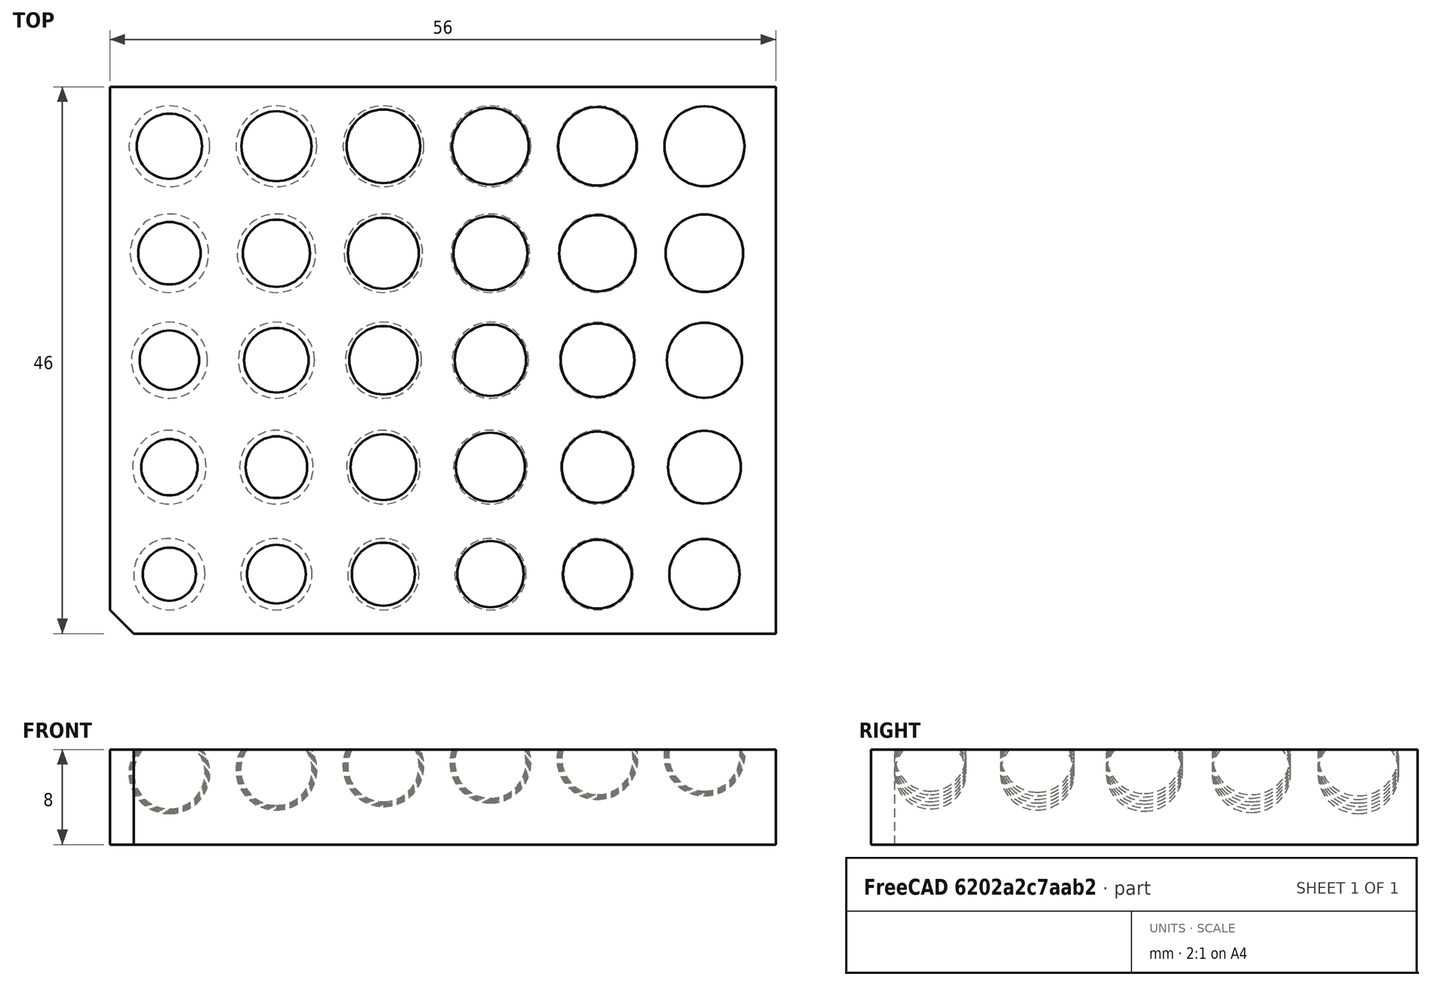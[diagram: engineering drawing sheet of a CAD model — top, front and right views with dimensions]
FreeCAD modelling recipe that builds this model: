
FCSTD DOCUMENT  (FreeCAD 0.18.4R)
Label: ball-socket-test
License: All rights reserved
LicenseURL: http://en.wikipedia.org/wiki/All_rights_reserved
objects: Part::Cut×30, Part::Feature×25, Part::Sphere×5, Part::Box×1, Part::Chamfer×1
note: 62 computed .brp shape members not serialized (recipe doc carries the construction recipe); baked Part::Feature solids carry a one-line shape summary decoded from their .brp

FEATURE [Part::Feature] Sphere006002
  Placement = pos=(18,9,6.6) rot=(0,0,1;0rad)
  shape: bbox 6.2 x 6.2 x 6.2 mm, 1 faces (baked)
FEATURE [Part::Feature] Sphere006001
  Placement = pos=(9,9,6.3) rot=(0,0,1;0rad)
  shape: bbox 6.2 x 6.2 x 6.2 mm, 1 faces (baked)
FEATURE [Part::Feature] Sphere005
  Placement = pos=(45,0,7.5) rot=(0,0,1;0rad)
  shape: bbox 6 x 6 x 6 mm, 1 faces (baked)
FEATURE [Part::Feature] Sphere001
  Placement = pos=(9,0,6.3) rot=(0,0,1;0rad)
  shape: bbox 6 x 6 x 6 mm, 1 faces (baked)
FEATURE [Part::Feature] Sphere002
  Placement = pos=(18,0,6.6) rot=(0,0,1;0rad)
  shape: bbox 6 x 6 x 6 mm, 1 faces (baked)
FEATURE [Part::Feature] Sphere004
  Placement = pos=(36,0,7.2) rot=(0,0,1;0rad)
  shape: bbox 6 x 6 x 6 mm, 1 faces (baked)
FEATURE [Part::Feature] Sphere003
  Placement = pos=(27,0,6.9) rot=(0,0,1;0rad)
  shape: bbox 6 x 6 x 6 mm, 1 faces (baked)
FEATURE [Part::Sphere] Sphere
  Angle1 = -90
  Angle2 = 90
  Angle3 = 360
  AttacherType = Attacher::AttachEngine3D
  Placement = pos=(0,0,6) rot=(0,0,1;0rad)
  Radius = 3
FEATURE [Part::Box] Box112015002017004007003  label="Cube089"
  AttacherType = Attacher::AttachEngine3D
  Height = 8
  Length = 56
  Placement = pos=(-5,-5,0) rot=(0,0,1;0rad)
  Width = 46
FEATURE [Part::Cut] Cut175
  Base = -> Box112015002017004007003
  Tool = -> Sphere
FEATURE [Part::Sphere] Sphere006
  Angle1 = -90
  Angle2 = 90
  Angle3 = 360
  AttacherType = Attacher::AttachEngine3D
  Placement = pos=(0,9,6) rot=(0,0,1;0rad)
  Radius = 3.1
FEATURE [Part::Feature] Sphere006003
  Placement = pos=(27,9,6.9) rot=(0,0,1;0rad)
  shape: bbox 6.2 x 6.2 x 6.2 mm, 1 faces (baked)
FEATURE [Part::Feature] Sphere006004
  Placement = pos=(36,9,7.2) rot=(0,0,1;0rad)
  shape: bbox 6.2 x 6.2 x 6.2 mm, 1 faces (baked)
FEATURE [Part::Feature] Sphere006005
  Placement = pos=(45,9,7.5) rot=(0,0,1;0rad)
  shape: bbox 6.2 x 6.2 x 6.2 mm, 1 faces (baked)
FEATURE [Part::Sphere] Sphere006006
  Angle1 = -90
  Angle2 = 90
  Angle3 = 360
  AttacherType = Attacher::AttachEngine3D
  Placement = pos=(0,18,6) rot=(0,0,1;0rad)
  Radius = 3.2
FEATURE [Part::Feature] Sphere006006001 .. Sphere006006005  x5 (patterned run collapsed; names and placements below)
  shape: bbox 6.4 x 6.4 x 6.4 mm, 1 faces (baked)
  placements: 5 in arithmetic series — first pos=(9,18,6.3) rot=(0,0,1;0rad), step (9,0,0.3), last pos=(45,18,7.5) rot=(0,0,1;0rad)
FEATURE [Part::Sphere] Sphere006006006
  Angle1 = -90
  Angle2 = 90
  Angle3 = 360
  AttacherType = Attacher::AttachEngine3D
  Placement = pos=(0,27,6) rot=(0,0,1;0rad)
  Radius = 3.3
FEATURE [Part::Feature] Sphere006006006001 .. Sphere006006006005  x5 (patterned run collapsed; names and placements below)
  shape: bbox 6.6 x 6.6 x 6.6 mm, 1 faces (baked)
  placements: 5 in arithmetic series — first pos=(9,27,6.3) rot=(0,0,1;0rad), step (9,0,0.3), last pos=(45,27,7.5) rot=(0,0,1;0rad)
FEATURE [Part::Sphere] Sphere006006006006
  Angle1 = -90
  Angle2 = 90
  Angle3 = 360
  AttacherType = Attacher::AttachEngine3D
  Placement = pos=(0,36,6) rot=(0,0,1;0rad)
  Radius = 3.4
FEATURE [Part::Feature] Sphere006006006006001 .. Sphere006006006006005  x5 (patterned run collapsed; names and placements below)
  shape: bbox 6.8 x 6.8 x 6.8 mm, 1 faces (baked)
  placements: 5 in arithmetic series — first pos=(9,36,6.3) rot=(0,0,1;0rad), step (9,0,0.3), last pos=(45,36,7.5) rot=(0,0,1;0rad)
FEATURE [Part::Cut] Cut176
  Base = -> Cut175
  Tool = -> Sphere006006006006005
FEATURE [Part::Cut] Cut177
  Base = -> Cut176
  Tool = -> Sphere006006006006004
FEATURE [Part::Cut] Cut178
  Base = -> Cut177
  Tool = -> Sphere006006006006003
FEATURE [Part::Cut] Cut179
  Base = -> Cut178
  Tool = -> Sphere006006006006002
FEATURE [Part::Cut] Cut180
  Base = -> Cut179
  Tool = -> Sphere006006006006001
FEATURE [Part::Cut] Cut181
  Base = -> Cut180
  Tool = -> Sphere006006006006
FEATURE [Part::Cut] Cut182
  Base = -> Cut181
  Tool = -> Sphere006006006005
FEATURE [Part::Cut] Cut183
  Base = -> Cut182
  Tool = -> Sphere006006006004
FEATURE [Part::Cut] Cut184
  Base = -> Cut183
  Tool = -> Sphere006006006003
FEATURE [Part::Cut] Cut185
  Base = -> Cut184
  Tool = -> Sphere006006006002
FEATURE [Part::Cut] Cut186
  Base = -> Cut185
  Tool = -> Sphere006006006001
FEATURE [Part::Cut] Cut187
  Base = -> Cut186
  Tool = -> Sphere006006006
FEATURE [Part::Cut] Cut188
  Base = -> Cut187
  Tool = -> Sphere006006005
FEATURE [Part::Cut] Cut189
  Base = -> Cut188
  Tool = -> Sphere006006004
FEATURE [Part::Cut] Cut190
  Base = -> Cut189
  Tool = -> Sphere006006003
FEATURE [Part::Cut] Cut191
  Base = -> Cut190
  Tool = -> Sphere006006002
FEATURE [Part::Cut] Cut192
  Base = -> Cut191
  Tool = -> Sphere006006001
FEATURE [Part::Cut] Cut193
  Base = -> Cut192
  Tool = -> Sphere006006
FEATURE [Part::Cut] Cut194
  Base = -> Cut193
  Tool = -> Sphere006005
FEATURE [Part::Cut] Cut195
  Base = -> Cut194
  Tool = -> Sphere006004
FEATURE [Part::Cut] Cut196
  Base = -> Cut195
  Tool = -> Sphere006003
FEATURE [Part::Cut] Cut197
  Base = -> Cut196
  Tool = -> Sphere006002
FEATURE [Part::Cut] Cut198
  Base = -> Cut197
  Tool = -> Sphere006001
FEATURE [Part::Cut] Cut199
  Base = -> Cut198
  Tool = -> Sphere006
FEATURE [Part::Cut] Cut200
  Base = -> Cut199
  Tool = -> Sphere005
FEATURE [Part::Cut] Cut201
  Base = -> Cut200
  Tool = -> Sphere004
FEATURE [Part::Cut] Cut202
  Base = -> Cut201
  Tool = -> Sphere003
FEATURE [Part::Cut] Cut203
  Base = -> Cut202
  Tool = -> Sphere002
FEATURE [Part::Cut] Cut204
  Base = -> Cut203
  Tool = -> Sphere001
FEATURE [Part::Chamfer] Chamfer006012003  label="ball-socket-test"
  Base = -> Cut204
  Edges = 1 edges r=2: [Edge1]
